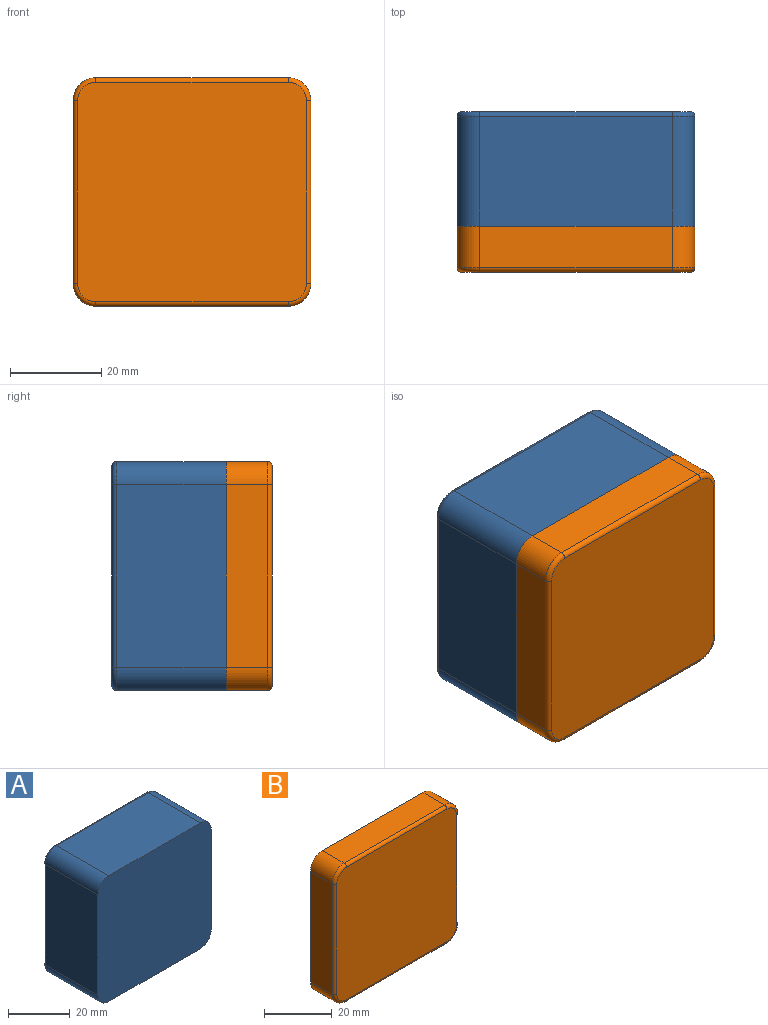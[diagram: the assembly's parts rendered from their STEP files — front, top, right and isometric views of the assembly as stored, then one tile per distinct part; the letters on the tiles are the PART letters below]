
ASSEMBLY  parts=2 mates=1
PART A: 22 faces, bbox 52.8x25x50.8 mm
  f0: plane 42x24mm, normal (0,0,-1), area 1001.7mm2, adj f4,f6,f9,f16,f18,f20
  f1: plane 40x24mm, normal (1,0,0), area 960mm2, adj f4,f6,f7,f15
  f2: plane 42x24mm, normal (0,0,1), area 1008mm2, adj f4,f7,f8,f11
  f3: plane 40x24mm, normal (-1,0,0), area 960mm2, adj f4,f8,f9,f12
  f4: plane 52x50mm, normal (0,-1,0), area 2578.5mm2, adj f0,f1,f2,f3,f6,f7,f8,f9
  f5: plane 50x48mm, normal (0,1,0), area 2386.3mm2, adj f10,f11,f12,f13,f14,f15,f16,f17
  f6: cylinder r=5mm len=24mm, axis (0,-1,0), area 188.5mm2, adj f0,f1,f4,f17
  f7: cylinder r=5mm len=24mm, axis (0,1,0), area 188.5mm2, adj f1,f2,f4,f13
  f8: cylinder r=5mm len=24mm, axis (0,-1,0), area 188.5mm2, adj f2,f3,f4,f10
  f9: cylinder r=5mm len=24mm, axis (0,1,0), area 188.5mm2, adj f0,f3,f4,f14
  f10: torus R=4mm, axis (0,-1,0), area 11.4mm2, adj f5,f8,f11,f12
  f11: cylinder r=1mm len=42mm, axis (-1,0,0), area 66mm2, adj f2,f5,f10,f13
  f12: cylinder r=1mm len=40mm, axis (0,0,-1), area 62.8mm2, adj f3,f5,f10,f14
  f13: torus R=4mm, axis (0,-1,0), area 11.4mm2, adj f5,f7,f11,f15
  f14: torus R=4mm, axis (0,-1,0), area 11.4mm2, adj f5,f9,f12,f16
  f15: cylinder r=1mm len=40mm, axis (0,0,1), area 62.8mm2, adj f1,f5,f13,f17
  f16: cylinder r=1mm len=42mm, axis (1,0,0), area 66mm2, adj f0,f5,f14,f17
  f17: torus R=4mm, axis (0,-1,0), area 11.4mm2, adj f5,f6,f15,f16
  f18: cylinder r=1mm len=25mm, axis (0,0,-1), area 157.1mm2, adj f0,f19
  f19: plane 2x2mm, normal (0,0,-1), area 3.1mm2, adj f18
  f20: cylinder r=1mm len=25mm, axis (0,0,-1), area 157.1mm2, adj f0,f21
  f21: plane 2x2mm, normal (0,0,-1), area 3.1mm2, adj f20
PART B: 18 faces, bbox 52.8x10x50.8 mm
  f0: plane 42x9mm, normal (0,0,-1), area 378mm2, adj f5,f6,f9,f15
  f1: plane 40x9mm, normal (1,0,0), area 360mm2, adj f5,f6,f7,f16
  f2: plane 42x9mm, normal (0,0,1), area 378mm2, adj f5,f7,f8,f12
  f3: plane 40x9mm, normal (-1,0,0), area 360mm2, adj f5,f8,f9,f11
  f4: plane 50x48mm, normal (0,-1,0), area 2386.3mm2, adj f10,f11,f12,f13,f14,f15,f16,f17
  f5: plane 52x50mm, normal (0,1,0), area 2578.5mm2, adj f0,f1,f2,f3,f6,f7,f8,f9
  f6: cylinder r=5mm len=9mm, axis (0,-1,0), area 70.7mm2, adj f0,f1,f5,f17
  f7: cylinder r=5mm len=9mm, axis (0,1,0), area 70.7mm2, adj f1,f2,f5,f14
  f8: cylinder r=5mm len=9mm, axis (0,-1,0), area 70.7mm2, adj f2,f3,f5,f10
  f9: cylinder r=5mm len=9mm, axis (0,1,0), area 70.7mm2, adj f0,f3,f5,f13
  f10: torus R=4mm, axis (0,-1,0), area 11.4mm2, adj f4,f8,f11,f12
  f11: cylinder r=1mm len=40mm, axis (0,0,1), area 62.8mm2, adj f3,f4,f10,f13
  f12: cylinder r=1mm len=42mm, axis (1,0,0), area 66mm2, adj f2,f4,f10,f14
  f13: torus R=4mm, axis (0,-1,0), area 11.4mm2, adj f4,f9,f11,f15
  f14: torus R=4mm, axis (0,-1,0), area 11.4mm2, adj f4,f7,f12,f16
  f15: cylinder r=1mm len=42mm, axis (-1,0,0), area 66mm2, adj f0,f4,f13,f17
  f16: cylinder r=1mm len=40mm, axis (0,0,-1), area 62.8mm2, adj f1,f4,f14,f17
  f17: torus R=4mm, axis (0,-1,0), area 11.4mm2, adj f4,f6,f15,f16
PLACE A t=(0,0.5,25)mm
PLACE B t=(0,0.5,25)mm
MATE fastened A.f4 <-> B.f5  axis (0,-1,0) through (0,-12,25)mm
